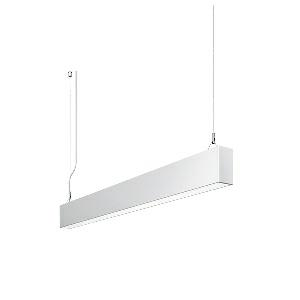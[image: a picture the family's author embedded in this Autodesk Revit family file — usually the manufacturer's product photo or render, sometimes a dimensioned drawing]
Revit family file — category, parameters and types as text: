
# Revit family: idoo_line_-_ilp_3000_830_d_00805721_7633
name_source: partatom
category: Lighting Fixtures
units: mm (PartAtom-declared; Revit-internal decimal feet)

## family parameters
Cut with Voids When Loaded = No
Host = Face
Light Source = No
Part Type = Normal
Room Calculation Point = No
Round Connector Dimension = Use Diameter
Shared = No

## types (1)
- IDOO.line - ILP 3000/830/D (1 x LED, 3000 lm, 3000K)
    Apparent Load = 23 VA
    Approval mark = CE
    CIE Flux Codes = 66 91 98 40 100
    Color Rendering = 80-89
    Color Temperature = 3000K
    Control Gear = Electronic ballast
    Default Elevation = 1800 mm
    Description = ILP 3000/830/D|Suspended luminaire|light source: LED|connected load: 220-240 V, 50/60 Hz|Power consumption: approx. 23 W|standby: approx. 0,20|luminous flux: 3000 lm|luminous efficacy: 130 lm/W|light distribution: Direct/indirect|direct ratio: approx. 40 %|colour temperature: Warm white, ca. 3000 K|color rendering index (CRI): >= 80|chromaticity tolerance:  3 SDCM|System of protection: IP 40|technology: Continuously dimmable|luminaire body|material: Sectional aluminium|colour: White|lamp cover: Acrylic (PMMA), Clear|mains lead: 2.00 m With free stranded wires|Fastening: Steel cable 0.3 - 0.7 m|glare control: Prism aperture|luminance(L65): <= 2700 cd/m|unified glare rating(4H 8H): <=  16|special features: DALI Load 1x, TouchDIM - dimming via standard switch, Flicker-free, Suitable as emergency lighting|
    Frequency = 50 Hz
    Height = 110 mm
    Lamp = 1 x LED
    Lamp Light Flux = 3000 lm
    Lamp count = 1
    Length = 1134 mm
    Luminous efficacy = 130 lm/W
    Manufacturer = Waldmann
    ModVariant = No
    Model = 00805721
    Mounting Place = Ceiling
    Mounting Type = Pendant
    Number of Poles = 1
    OnlyDefault = Yes
    Power Factor = 1
    Product Name = IDOO.line - ILP 3000/830/D
    Product group = Suspended luminaire
    ProductGroupID = 9
    Protection Class = Protection class I
    Protection Degree = IP 40
    RLX_Detail_Level = 1
    RLX_Emergency_Light_Flux = 0 lm
    RLX_Emergency_Type = 0
    RLX_Emergency_Type_DB = No
    RlxData = <blob elided: 18937 chars, md5=a990408d>
    Socket = socket
    Standby Power = 0 W
    System Light Flux = 3000 lm
    System Power = 23 W
    Type Comments = Product without accessories
    Type Image = 113289000-00692516.jpg
    URL = http://relux.com
    VarID = ---
    Voltage = 230 V
    Voltage Range = 220-240 V
    Weight = 0.00 kg
    Width = 60 mm  [stored 0.19685 ft]

note: [stored X ft] marks values corroborated as IEEE doubles in the binary element streams (Revit-internal decimal feet)

## geometry (parser evidence)
native form markers: Blend x4, Sweep x14
no freeform markers — native parametric forms only
